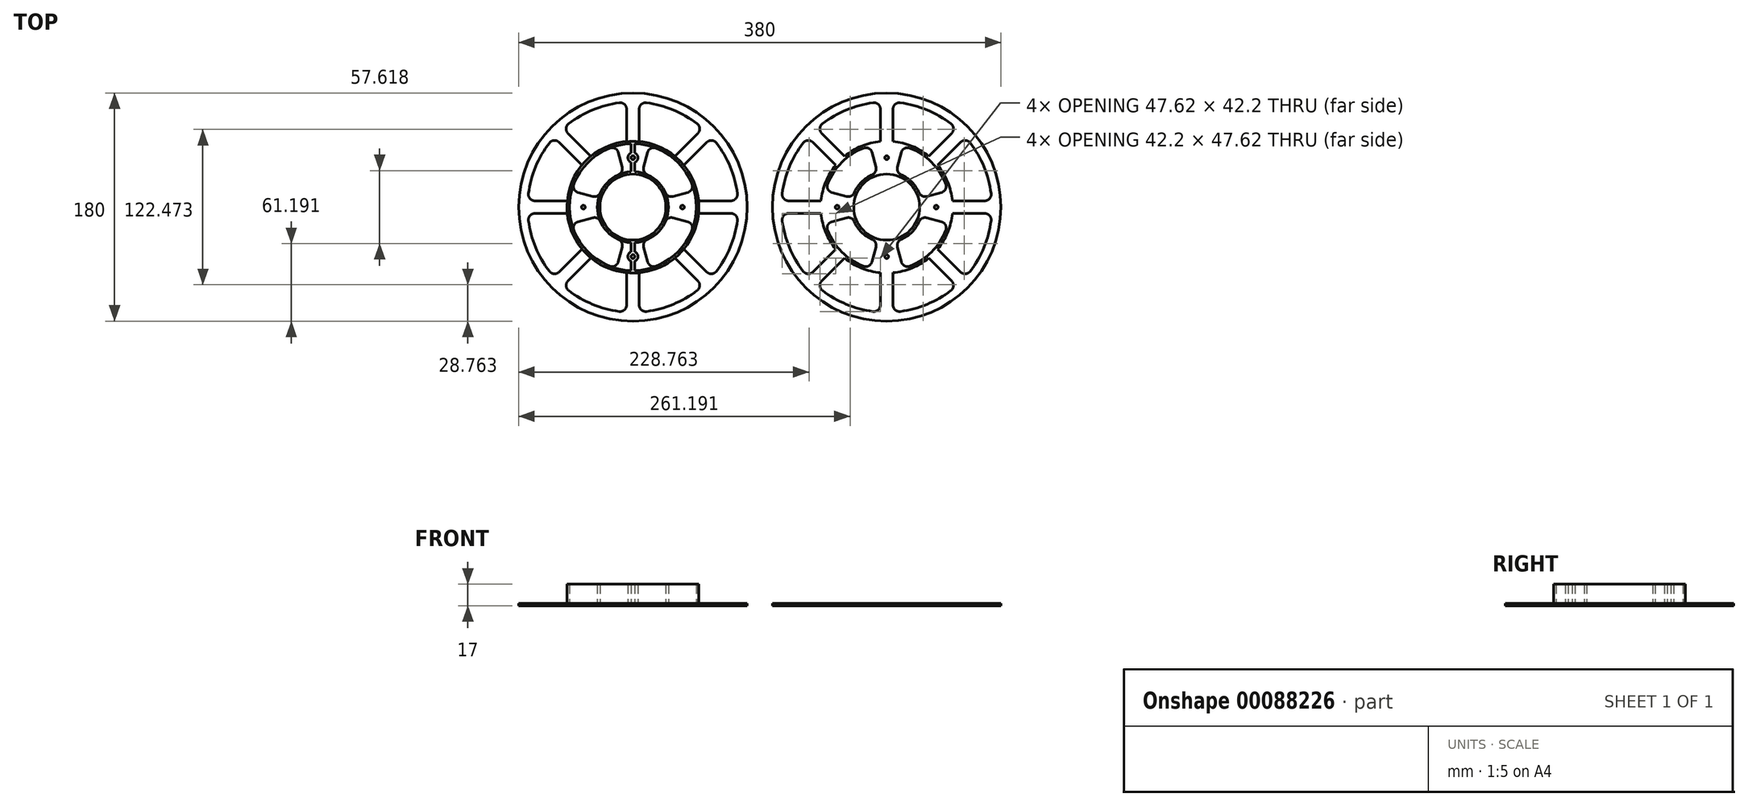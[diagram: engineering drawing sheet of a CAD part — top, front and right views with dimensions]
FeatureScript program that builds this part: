
annotation { "Feature Type Name" : "Feature", "Feature Type Description" : "" }
export const myFeature = defineFeature(function(context is Context, id is Id, definition is map)
    precondition{}
    {
        {
            var Q0;
            Q0=qCreatedBy(makeId("Top.planeOp"),FACE);
            var sketch = newSketch(context, id + "F0", { "sketchPlane" : qUnion([Q0])});
            skCircle(sketch, "E0", {"center": v(0, 0) * mm, "radius": 26 * mm});
            skArc(sketch, "E1", {"start": v(51.76, 5) * mm, "mid": v(48.04, 19.9) * mm, "end": v(40.13, 33.06) * mm});
            skCircle(sketch, "E2", {"center": v(0, 0) * mm, "radius": 90 * mm});
            skArc(sketch, "E3", {"start": v(-11.26, 25.64) * mm, "mid": v(-19.8, 19.8) * mm, "end": v(-25.64, 11.26) * mm});
            skArc(sketch, "E4", {"start": v(-18.23, 46.56) * mm, "mid": v(-35.36, 35.36) * mm, "end": v(-46.56, 18.23) * mm});
            skCircle(sketch, "E5", {"center": v(0, 39) * mm, "radius": 1.5 * mm});
            skCircle(sketch, "E6.1.1", {"center": v(39, 0) * mm, "radius": 1.5 * mm});
            skCircle(sketch, "E6.2.1", {"center": v(0, -39) * mm, "radius": 1.5 * mm});
            skCircle(sketch, "E6.3.1", {"center": v(-39, 0) * mm, "radius": 1.5 * mm});
            skArc(sketch, "E7.0", {"start": v(82.32, 10.64) * mm, "mid": v(76.68, 31.76) * mm, "end": v(65.73, 50.68) * mm});
            skLineSegment(sketch, "E8.0", {"start": v(-5, 77.36) * mm, "end": v(-5, 51.76) * mm});
            skLineSegment(sketch, "E9.0", {"start": v(5, 77.36) * mm, "end": v(5, 51.76) * mm});
            skLineSegment(sketch, "E10.1.0", {"start": v(-51.16, 58.23) * mm, "end": v(-33.06, 40.13) * mm});
            skLineSegment(sketch, "E10.1.1", {"start": v(-58.23, 51.16) * mm, "end": v(-40.13, 33.06) * mm});
            skLineSegment(sketch, "E10.2.0", {"start": v(-77.36, 5) * mm, "end": v(-51.76, 5) * mm});
            skLineSegment(sketch, "E10.2.1", {"start": v(-77.36, -5) * mm, "end": v(-51.76, -5) * mm});
            skLineSegment(sketch, "E10.3.0", {"start": v(-58.23, -51.16) * mm, "end": v(-40.13, -33.06) * mm});
            skLineSegment(sketch, "E10.3.1", {"start": v(-51.16, -58.23) * mm, "end": v(-33.06, -40.13) * mm});
            skLineSegment(sketch, "E10.4.0", {"start": v(-5, -77.36) * mm, "end": v(-5, -51.76) * mm});
            skLineSegment(sketch, "E10.4.1", {"start": v(5, -77.36) * mm, "end": v(5, -51.76) * mm});
            skLineSegment(sketch, "E10.5.0", {"start": v(51.16, -58.23) * mm, "end": v(33.06, -40.13) * mm});
            skLineSegment(sketch, "E10.5.1", {"start": v(58.23, -51.16) * mm, "end": v(40.13, -33.06) * mm});
            skLineSegment(sketch, "E10.6.0", {"start": v(77.36, -5) * mm, "end": v(51.76, -5) * mm});
            skLineSegment(sketch, "E10.6.1", {"start": v(77.36, 5) * mm, "end": v(51.76, 5) * mm});
            skLineSegment(sketch, "E10.7.0", {"start": v(58.23, 51.16) * mm, "end": v(40.13, 33.06) * mm});
            skLineSegment(sketch, "E10.7.1", {"start": v(51.16, 58.23) * mm, "end": v(33.06, 40.13) * mm});
            skLineSegment(sketch, "E11.1.0", {"start": v(-8.44, 31.5) * mm, "end": v(-11.57, 43.2) * mm});
            skLineSegment(sketch, "E12.1.5.0", {"start": v(-31.5, 8.44) * mm, "end": v(-43.2, 11.57) * mm});
            skLineSegment(sketch, "E12.1.7.0", {"start": v(-31.5, -8.44) * mm, "end": v(-43.2, -11.57) * mm});
            skLineSegment(sketch, "E13.1.11.0", {"start": v(-8.44, -31.5) * mm, "end": v(-11.57, -43.2) * mm});
            skLineSegment(sketch, "E13.1.13.0", {"start": v(8.44, -31.5) * mm, "end": v(11.57, -43.2) * mm});
            skLineSegment(sketch, "E14.1.17.0", {"start": v(31.5, -8.44) * mm, "end": v(43.2, -11.57) * mm});
            skLineSegment(sketch, "E14.1.19.0", {"start": v(31.5, 8.44) * mm, "end": v(43.2, 11.57) * mm});
            skLineSegment(sketch, "E14.1.23.0", {"start": v(8.44, 31.5) * mm, "end": v(11.57, 43.2) * mm});
            skArc(sketch, "E15.trimOffspring", {"start": v(46.56, 18.23) * mm, "mid": v(35.36, 35.36) * mm, "end": v(18.23, 46.56) * mm});
            skArc(sketch, "E16.trimOffspring", {"start": v(25.64, 11.26) * mm, "mid": v(19.8, 19.8) * mm, "end": v(11.26, 25.64) * mm});
            skArc(sketch, "E17.trimOffspring", {"start": v(11.26, -25.64) * mm, "mid": v(19.8, -19.8) * mm, "end": v(25.64, -11.26) * mm});
            skArc(sketch, "E18.trimOffspring", {"start": v(18.23, -46.56) * mm, "mid": v(35.36, -35.36) * mm, "end": v(46.56, -18.23) * mm});
            skArc(sketch, "E19.trimOffspring", {"start": v(50.68, 65.73) * mm, "mid": v(31.76, 76.68) * mm, "end": v(10.64, 82.32) * mm});
            skArc(sketch, "E20.trimOffspring", {"start": v(33.06, 40.13) * mm, "mid": v(19.9, 48.04) * mm, "end": v(5, 51.76) * mm});
            skArc(sketch, "E21.trimOffspring", {"start": v(-10.64, 82.32) * mm, "mid": v(-31.76, 76.68) * mm, "end": v(-50.68, 65.73) * mm});
            skArc(sketch, "E22.trimOffspring", {"start": v(-5, 51.76) * mm, "mid": v(-19.9, 48.04) * mm, "end": v(-33.06, 40.13) * mm});
            skArc(sketch, "E23.trimOffspring", {"start": v(-40.13, 33.06) * mm, "mid": v(-48.04, 19.9) * mm, "end": v(-51.76, 5) * mm});
            skArc(sketch, "E24.trimOffspring", {"start": v(-65.73, 50.68) * mm, "mid": v(-76.68, 31.76) * mm, "end": v(-82.32, 10.64) * mm});
            skArc(sketch, "E25.trimOffspring", {"start": v(-82.32, -10.64) * mm, "mid": v(-76.68, -31.76) * mm, "end": v(-65.73, -50.68) * mm});
            skArc(sketch, "E26.trimOffspring", {"start": v(-50.68, -65.73) * mm, "mid": v(-31.76, -76.68) * mm, "end": v(-10.64, -82.32) * mm});
            skArc(sketch, "E27.trimOffspring", {"start": v(10.64, -82.32) * mm, "mid": v(31.76, -76.68) * mm, "end": v(50.68, -65.73) * mm});
            skArc(sketch, "E28.trimOffspring", {"start": v(65.73, -50.68) * mm, "mid": v(76.68, -31.76) * mm, "end": v(82.32, -10.64) * mm});
            skArc(sketch, "E29.trimOffspring", {"start": v(40.13, -33.06) * mm, "mid": v(48.04, -19.9) * mm, "end": v(51.76, -5) * mm});
            skArc(sketch, "E30.trimOffspring", {"start": v(5, -51.76) * mm, "mid": v(19.9, -48.04) * mm, "end": v(33.06, -40.13) * mm});
            skArc(sketch, "E31.trimOffspring", {"start": v(-33.06, -40.13) * mm, "mid": v(-19.9, -48.04) * mm, "end": v(-5, -51.76) * mm});
            skArc(sketch, "E32.trimOffspring", {"start": v(-46.56, -18.23) * mm, "mid": v(-35.36, -35.36) * mm, "end": v(-18.23, -46.56) * mm});
            skArc(sketch, "E33.trimOffspring", {"start": v(-51.76, -5) * mm, "mid": v(-48.04, -19.9) * mm, "end": v(-40.13, -33.06) * mm});
            skArc(sketch, "E34.trimOffspring", {"start": v(-25.64, -11.26) * mm, "mid": v(-19.8, -19.8) * mm, "end": v(-11.26, -25.64) * mm});
            skPoint(sketch, "E35.visualSharp", {"position": v(-5, 82.85) * mm});
            skArc(sketch, "E35.filletArc", {"start": v(-5, 77.36) * mm, "mid": v(-6.7, 81.11) * mm, "end": v(-10.64, 82.32) * mm});
            skPoint(sketch, "E36.visualSharp", {"position": v(-55.05, 62.12) * mm});
            skArc(sketch, "E36.filletArc", {"start": v(-50.68, 65.73) * mm, "mid": v(-52.62, 62.1) * mm, "end": v(-51.16, 58.23) * mm});
            skPoint(sketch, "E37.visualSharp", {"position": v(-7.25, 27.05) * mm});
            skArc(sketch, "E37.filletArc", {"start": v(-11.26, 25.64) * mm, "mid": v(-8.76, 28.05) * mm, "end": v(-8.44, 31.5) * mm});
            skPoint(sketch, "E38.visualSharp", {"position": v(-27.05, 7.25) * mm});
            skArc(sketch, "E38.filletArc", {"start": v(-31.5, 8.44) * mm, "mid": v(-28.05, 8.76) * mm, "end": v(-25.64, 11.26) * mm});
            skPoint(sketch, "E39.visualSharp", {"position": v(7.25, 27.05) * mm});
            skArc(sketch, "E39.filletArc", {"start": v(8.44, 31.5) * mm, "mid": v(8.76, 28.05) * mm, "end": v(11.26, 25.64) * mm});
            skPoint(sketch, "E40.visualSharp", {"position": v(12.94, 48.3) * mm});
            skArc(sketch, "E40.filletArc", {"start": v(18.23, 46.56) * mm, "mid": v(14.15, 46.37) * mm, "end": v(11.57, 43.2) * mm});
            skPoint(sketch, "E41.visualSharp", {"position": v(48.3, 12.94) * mm});
            skArc(sketch, "E41.filletArc", {"start": v(43.2, 11.57) * mm, "mid": v(46.37, 14.15) * mm, "end": v(46.56, 18.23) * mm});
            skPoint(sketch, "E42.visualSharp", {"position": v(27.05, 7.25) * mm});
            skArc(sketch, "E42.filletArc", {"start": v(25.64, 11.26) * mm, "mid": v(28.05, 8.76) * mm, "end": v(31.5, 8.44) * mm});
            skPoint(sketch, "E43.visualSharp", {"position": v(-12.94, 48.3) * mm});
            skArc(sketch, "E43.filletArc", {"start": v(-11.57, 43.2) * mm, "mid": v(-14.15, 46.37) * mm, "end": v(-18.23, 46.56) * mm});
            skPoint(sketch, "E44.visualSharp", {"position": v(-48.3, 12.94) * mm});
            skArc(sketch, "E44.filletArc", {"start": v(-46.56, 18.23) * mm, "mid": v(-46.37, 14.15) * mm, "end": v(-43.2, 11.57) * mm});
            skPoint(sketch, "E45.visualSharp", {"position": v(-27.05, -7.25) * mm});
            skArc(sketch, "E45.filletArc", {"start": v(-25.64, -11.26) * mm, "mid": v(-28.05, -8.76) * mm, "end": v(-31.5, -8.44) * mm});
            skPoint(sketch, "E46.visualSharp", {"position": v(-48.3, -12.94) * mm});
            skArc(sketch, "E46.filletArc", {"start": v(-43.2, -11.57) * mm, "mid": v(-46.37, -14.15) * mm, "end": v(-46.56, -18.23) * mm});
            skPoint(sketch, "E47.visualSharp", {"position": v(-12.94, -48.3) * mm});
            skArc(sketch, "E47.filletArc", {"start": v(-18.23, -46.56) * mm, "mid": v(-14.15, -46.37) * mm, "end": v(-11.57, -43.2) * mm});
            skPoint(sketch, "E48.visualSharp", {"position": v(-7.25, -27.05) * mm});
            skArc(sketch, "E48.filletArc", {"start": v(-8.44, -31.5) * mm, "mid": v(-8.76, -28.05) * mm, "end": v(-11.26, -25.64) * mm});
            skPoint(sketch, "E49.visualSharp", {"position": v(7.25, -27.05) * mm});
            skArc(sketch, "E49.filletArc", {"start": v(11.26, -25.64) * mm, "mid": v(8.76, -28.05) * mm, "end": v(8.44, -31.5) * mm});
            skPoint(sketch, "E50.visualSharp", {"position": v(48.3, -12.94) * mm});
            skArc(sketch, "E50.filletArc", {"start": v(46.56, -18.23) * mm, "mid": v(46.37, -14.15) * mm, "end": v(43.2, -11.57) * mm});
            skPoint(sketch, "E51.visualSharp", {"position": v(27.05, -7.25) * mm});
            skArc(sketch, "E51.filletArc", {"start": v(31.5, -8.44) * mm, "mid": v(28.05, -8.76) * mm, "end": v(25.64, -11.26) * mm});
            skPoint(sketch, "E52.visualSharp", {"position": v(12.94, -48.3) * mm});
            skArc(sketch, "E52.filletArc", {"start": v(11.57, -43.2) * mm, "mid": v(14.15, -46.37) * mm, "end": v(18.23, -46.56) * mm});
            skPoint(sketch, "E53.visualSharp", {"position": v(5, 82.85) * mm});
            skArc(sketch, "E53.filletArc", {"start": v(10.64, 82.32) * mm, "mid": v(6.7, 81.11) * mm, "end": v(5, 77.36) * mm});
            skPoint(sketch, "E54.visualSharp", {"position": v(55.05, 62.12) * mm});
            skArc(sketch, "E54.filletArc", {"start": v(51.16, 58.23) * mm, "mid": v(52.62, 62.1) * mm, "end": v(50.68, 65.73) * mm});
            skPoint(sketch, "E55.visualSharp", {"position": v(62.12, 55.05) * mm});
            skArc(sketch, "E55.filletArc", {"start": v(65.73, 50.68) * mm, "mid": v(62.1, 52.62) * mm, "end": v(58.23, 51.16) * mm});
            skPoint(sketch, "E56.visualSharp", {"position": v(82.85, -5) * mm});
            skArc(sketch, "E56.filletArc", {"start": v(82.32, -10.64) * mm, "mid": v(81.11, -6.7) * mm, "end": v(77.36, -5) * mm});
            skPoint(sketch, "E57.visualSharp", {"position": v(82.85, 5) * mm});
            skArc(sketch, "E57.filletArc", {"start": v(77.36, 5) * mm, "mid": v(81.11, 6.7) * mm, "end": v(82.32, 10.64) * mm});
            skPoint(sketch, "E58.visualSharp", {"position": v(62.12, -55.05) * mm});
            skArc(sketch, "E58.filletArc", {"start": v(58.23, -51.16) * mm, "mid": v(62.1, -52.62) * mm, "end": v(65.73, -50.68) * mm});
            skPoint(sketch, "E59.visualSharp", {"position": v(55.05, -62.12) * mm});
            skArc(sketch, "E59.filletArc", {"start": v(50.68, -65.73) * mm, "mid": v(52.62, -62.1) * mm, "end": v(51.16, -58.23) * mm});
            skPoint(sketch, "E60.visualSharp", {"position": v(-5, -82.85) * mm});
            skArc(sketch, "E60.filletArc", {"start": v(-10.64, -82.32) * mm, "mid": v(-6.7, -81.11) * mm, "end": v(-5, -77.36) * mm});
            skPoint(sketch, "E61.visualSharp", {"position": v(5, -82.85) * mm});
            skArc(sketch, "E61.filletArc", {"start": v(5, -77.36) * mm, "mid": v(6.7, -81.11) * mm, "end": v(10.64, -82.32) * mm});
            skPoint(sketch, "E62.visualSharp", {"position": v(-55.05, -62.12) * mm});
            skArc(sketch, "E62.filletArc", {"start": v(-51.16, -58.23) * mm, "mid": v(-52.62, -62.1) * mm, "end": v(-50.68, -65.73) * mm});
            skPoint(sketch, "E63.visualSharp", {"position": v(-62.12, -55.05) * mm});
            skArc(sketch, "E63.filletArc", {"start": v(-65.73, -50.68) * mm, "mid": v(-62.1, -52.62) * mm, "end": v(-58.23, -51.16) * mm});
            skPoint(sketch, "E64.visualSharp", {"position": v(-82.85, -5) * mm});
            skArc(sketch, "E64.filletArc", {"start": v(-77.36, -5) * mm, "mid": v(-81.11, -6.7) * mm, "end": v(-82.32, -10.64) * mm});
            skPoint(sketch, "E65.visualSharp", {"position": v(-82.85, 5) * mm});
            skArc(sketch, "E65.filletArc", {"start": v(-82.32, 10.64) * mm, "mid": v(-81.11, 6.7) * mm, "end": v(-77.36, 5) * mm});
            skPoint(sketch, "E66.visualSharp", {"position": v(-62.12, 55.05) * mm});
            skArc(sketch, "E66.filletArc", {"start": v(-58.23, 51.16) * mm, "mid": v(-62.1, 52.62) * mm, "end": v(-65.73, 50.68) * mm});
            skSolve(sketch);
        }
        {
            var Q0;
            Q0=qCreatedBy(makeId("Top.planeOp"),FACE);
            var sketch = newSketch(context, id + "F1", { "sketchPlane" : qUnion([Q0])});
            skCircle(sketch, "E67", {"center": v(0, 0) * mm, "radius": 52 * mm});
            skCircle(sketch, "E68", {"center": v(0, 0) * mm, "radius": 26 * mm});
            skArc(sketch, "E69.0", {"start": v(-1.5, 27.96) * mm, "mid": v(-28, 0) * mm, "end": v(-1.5, -27.96) * mm});
            skArc(sketch, "E70.0", {"start": v(-1.5, 49.98) * mm, "mid": v(-50, 0) * mm, "end": v(-1.5, -49.98) * mm});
            skArc(sketch, "E71", {"start": v(-1.5, 42.7) * mm, "mid": v(-4, 39) * mm, "end": v(-1.5, 35.3) * mm});
            skCircle(sketch, "E72", {"center": v(0, 39) * mm, "radius": 1.5 * mm});
            skArc(sketch, "E73.1.0", {"start": v(-1.5, -35.3) * mm, "mid": v(-4, -39) * mm, "end": v(-1.5, -42.7) * mm});
            skCircle(sketch, "E73.1.1", {"center": v(0, -39) * mm, "radius": 1.5 * mm});
            skLineSegment(sketch, "E74", {"start": v(-1.5, 49.98) * mm, "end": v(-1.5, 42.7) * mm});
            skLineSegment(sketch, "E75.0", {"start": v(1.5, 49.98) * mm, "end": v(1.5, 42.7) * mm});
            skArc(sketch, "E76.trimOffspring", {"start": v(1.5, 35.3) * mm, "mid": v(4, 39) * mm, "end": v(1.5, 42.7) * mm});
            skLineSegment(sketch, "E77.trimOffspring", {"start": v(-1.5, 35.3) * mm, "end": v(-1.5, 27.96) * mm});
            skLineSegment(sketch, "E78.trimOffspring", {"start": v(1.5, 35.3) * mm, "end": v(1.5, 27.96) * mm});
            skLineSegment(sketch, "E79", {"start": v(-1.5, -35.3) * mm, "end": v(-1.5, -27.96) * mm});
            skLineSegment(sketch, "E80", {"start": v(-1.5, -42.7) * mm, "end": v(-1.5, -49.98) * mm});
            skLineSegment(sketch, "E81.0", {"start": v(1.5, -35.3) * mm, "end": v(1.5, -27.96) * mm});
            skLineSegment(sketch, "E81.1", {"start": v(1.5, -42.7) * mm, "end": v(1.5, -49.98) * mm});
            skArc(sketch, "E82.trimOffspring", {"start": v(1.5, -42.7) * mm, "mid": v(4, -39) * mm, "end": v(1.5, -35.3) * mm});
            skArc(sketch, "E83.trimOffspring", {"start": v(1.5, -49.98) * mm, "mid": v(50, 0) * mm, "end": v(1.5, 49.98) * mm});
            skArc(sketch, "E84.trimOffspring", {"start": v(1.5, -27.96) * mm, "mid": v(28, 0) * mm, "end": v(1.5, 27.96) * mm});
            skSolve(sketch);
        }
        {
            var Q0;
            Q0 = qSketchRegion(id + "F0", true);
            extrude(context, id + "F2", {"entities" : qUnion([Q0]), "depth" : 2 * mm});
        }
        {
            var Q0;
            Q0=makeQuery(id+"F2.opExtrude","SWEPT_BODY",BODY,{"disambiguationData":[OSD([sQuery(id+"F0.wireOp",EDGE,"E0"),sQuery(id+"F0.wireOp",EDGE,"E1"),sQuery(id+"F0.wireOp",EDGE,"E2"),sQuery(id+"F0.wireOp",EDGE,"E3"),sQuery(id+"F0.wireOp",EDGE,"E4"),sQuery(id+"F0.wireOp",EDGE,"E5"),sQuery(id+"F0.wireOp",EDGE,"E6.1.1"),sQuery(id+"F0.wireOp",EDGE,"E6.2.1"),sQuery(id+"F0.wireOp",EDGE,"E6.3.1"),sQuery(id+"F0.wireOp",EDGE,"E7.0"),sQuery(id+"F0.wireOp",EDGE,"E8.0"),sQuery(id+"F0.wireOp",EDGE,"E9.0"),sQuery(id+"F0.wireOp",EDGE,"E10.1.0"),sQuery(id+"F0.wireOp",EDGE,"E10.1.1"),sQuery(id+"F0.wireOp",EDGE,"E10.2.0"),sQuery(id+"F0.wireOp",EDGE,"E10.2.1"),sQuery(id+"F0.wireOp",EDGE,"E10.3.0"),sQuery(id+"F0.wireOp",EDGE,"E10.3.1"),sQuery(id+"F0.wireOp",EDGE,"E10.4.0"),sQuery(id+"F0.wireOp",EDGE,"E10.4.1"),sQuery(id+"F0.wireOp",EDGE,"E10.5.0"),sQuery(id+"F0.wireOp",EDGE,"E10.5.1"),sQuery(id+"F0.wireOp",EDGE,"E10.6.0"),sQuery(id+"F0.wireOp",EDGE,"E10.6.1"),sQuery(id+"F0.wireOp",EDGE,"E10.7.0"),sQuery(id+"F0.wireOp",EDGE,"E10.7.1"),sQuery(id+"F0.wireOp",EDGE,"E11.1.0"),sQuery(id+"F0.wireOp",EDGE,"E12.1.5.0"),sQuery(id+"F0.wireOp",EDGE,"E12.1.7.0"),sQuery(id+"F0.wireOp",EDGE,"E13.1.11.0"),sQuery(id+"F0.wireOp",EDGE,"E13.1.13.0"),sQuery(id+"F0.wireOp",EDGE,"E14.1.17.0"),sQuery(id+"F0.wireOp",EDGE,"E14.1.19.0"),sQuery(id+"F0.wireOp",EDGE,"E14.1.23.0"),sQuery(id+"F0.wireOp",EDGE,"E15.trimOffspring"),sQuery(id+"F0.wireOp",EDGE,"E16.trimOffspring"),sQuery(id+"F0.wireOp",EDGE,"E17.trimOffspring"),sQuery(id+"F0.wireOp",EDGE,"E18.trimOffspring"),sQuery(id+"F0.wireOp",EDGE,"E19.trimOffspring"),sQuery(id+"F0.wireOp",EDGE,"E20.trimOffspring"),sQuery(id+"F0.wireOp",EDGE,"E21.trimOffspring"),sQuery(id+"F0.wireOp",EDGE,"E22.trimOffspring"),sQuery(id+"F0.wireOp",EDGE,"E23.trimOffspring"),sQuery(id+"F0.wireOp",EDGE,"E24.trimOffspring"),sQuery(id+"F0.wireOp",EDGE,"E25.trimOffspring"),sQuery(id+"F0.wireOp",EDGE,"E26.trimOffspring"),sQuery(id+"F0.wireOp",EDGE,"E27.trimOffspring"),sQuery(id+"F0.wireOp",EDGE,"E28.trimOffspring"),sQuery(id+"F0.wireOp",EDGE,"E29.trimOffspring"),sQuery(id+"F0.wireOp",EDGE,"E30.trimOffspring"),sQuery(id+"F0.wireOp",EDGE,"E31.trimOffspring"),sQuery(id+"F0.wireOp",EDGE,"E32.trimOffspring"),sQuery(id+"F0.wireOp",EDGE,"E33.trimOffspring"),sQuery(id+"F0.wireOp",EDGE,"E34.trimOffspring"),sQuery(id+"F0.wireOp",EDGE,"E35.filletArc"),sQuery(id+"F0.wireOp",EDGE,"E36.filletArc"),sQuery(id+"F0.wireOp",EDGE,"E37.filletArc"),sQuery(id+"F0.wireOp",EDGE,"E38.filletArc"),sQuery(id+"F0.wireOp",EDGE,"E39.filletArc"),sQuery(id+"F0.wireOp",EDGE,"E40.filletArc"),sQuery(id+"F0.wireOp",EDGE,"E41.filletArc"),sQuery(id+"F0.wireOp",EDGE,"E42.filletArc"),sQuery(id+"F0.wireOp",EDGE,"E43.filletArc"),sQuery(id+"F0.wireOp",EDGE,"E44.filletArc"),sQuery(id+"F0.wireOp",EDGE,"E45.filletArc"),sQuery(id+"F0.wireOp",EDGE,"E46.filletArc"),sQuery(id+"F0.wireOp",EDGE,"E47.filletArc"),sQuery(id+"F0.wireOp",EDGE,"E48.filletArc"),sQuery(id+"F0.wireOp",EDGE,"E49.filletArc"),sQuery(id+"F0.wireOp",EDGE,"E50.filletArc"),sQuery(id+"F0.wireOp",EDGE,"E51.filletArc"),sQuery(id+"F0.wireOp",EDGE,"E52.filletArc"),sQuery(id+"F0.wireOp",EDGE,"E53.filletArc"),sQuery(id+"F0.wireOp",EDGE,"E54.filletArc"),sQuery(id+"F0.wireOp",EDGE,"E55.filletArc"),sQuery(id+"F0.wireOp",EDGE,"E56.filletArc"),sQuery(id+"F0.wireOp",EDGE,"E57.filletArc"),sQuery(id+"F0.wireOp",EDGE,"E58.filletArc"),sQuery(id+"F0.wireOp",EDGE,"E59.filletArc"),sQuery(id+"F0.wireOp",EDGE,"E60.filletArc"),sQuery(id+"F0.wireOp",EDGE,"E61.filletArc"),sQuery(id+"F0.wireOp",EDGE,"E62.filletArc"),sQuery(id+"F0.wireOp",EDGE,"E63.filletArc"),sQuery(id+"F0.wireOp",EDGE,"E64.filletArc"),sQuery(id+"F0.wireOp",EDGE,"E65.filletArc"),sQuery(id+"F0.wireOp",EDGE,"E66.filletArc")])]});
            transform(context, id + "F3", {"entities" : qUnion([Q0]), "transformType" : TransformType.TRANSLATION_3D, "dx" : 200 * mm, "dy" : 0 * mm, "dz" : 0 * mm, "makeCopy" : true});
        }
        {
            var Q0;
            Q0 = qSketchRegion(id + "F1", true);
            extrude(context, id + "F4", {"entities" : qUnion([Q0]), "operationType" : NewBodyOperationType.ADD, "depth" : 17 * mm});
        }
    });
